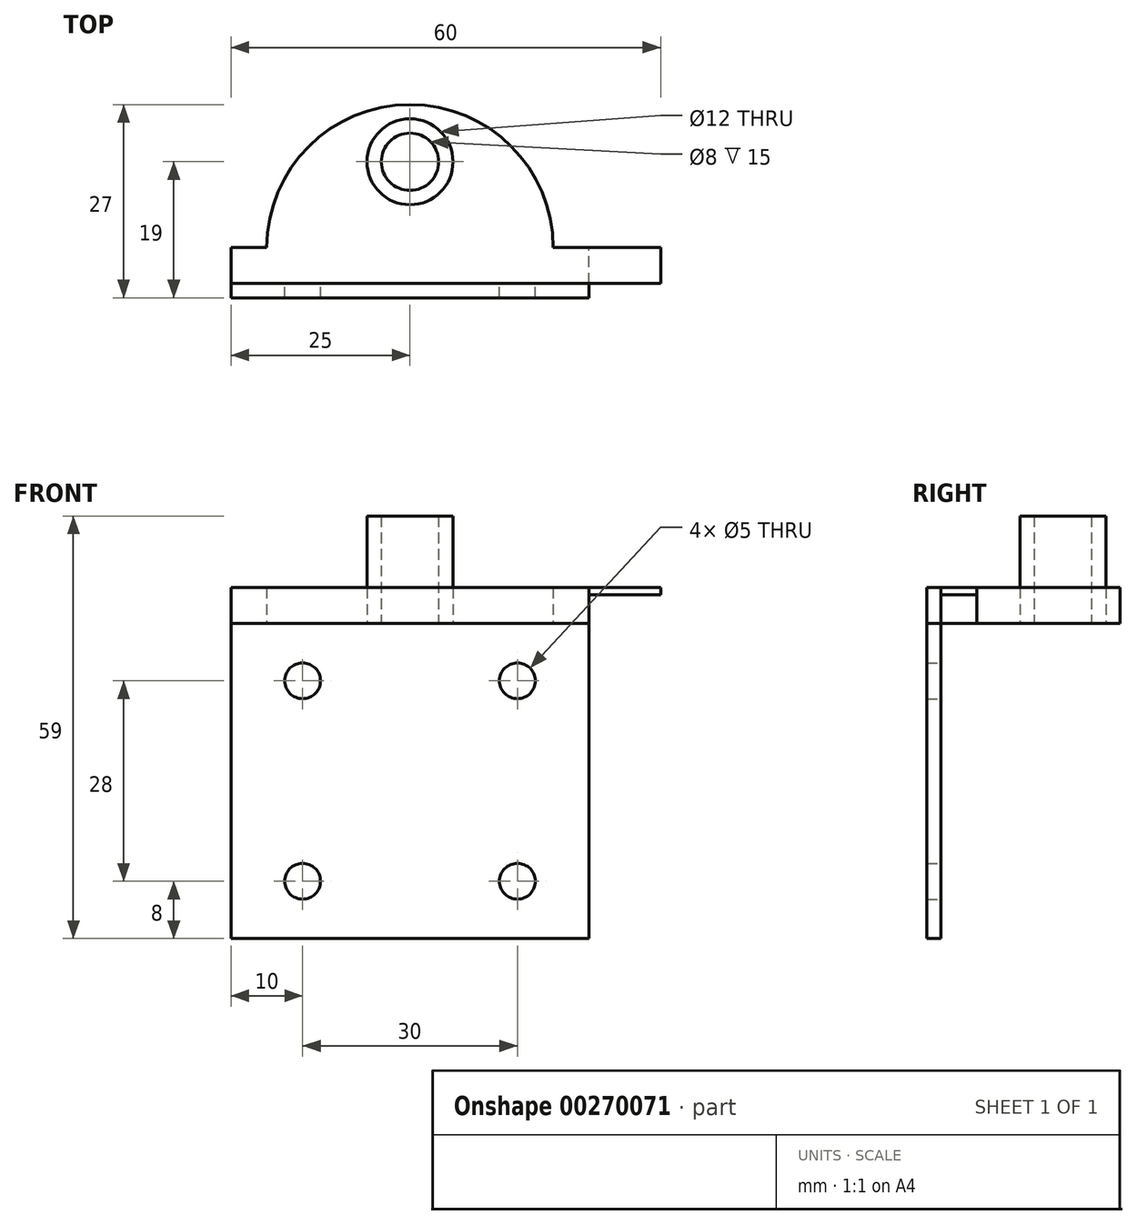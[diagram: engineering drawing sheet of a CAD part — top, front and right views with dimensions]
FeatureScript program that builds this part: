
annotation { "Feature Type Name" : "Feature", "Feature Type Description" : "" }
export const myFeature = defineFeature(function(context is Context, id is Id, definition is map)
    precondition{}
    {
        {
            var Q0;
            Q0=qCreatedBy(makeId("Front.planeOp"),FACE);
            var sketch = newSketch(context, id + "F0", { "sketchPlane" : qUnion([Q0])});
            skLineSegment(sketch, "E0.bottom", {"start": v(25, 22) * mm, "end": v(-25, 22) * mm});
            skLineSegment(sketch, "E0.top", {"start": v(25, -22) * mm, "end": v(-25, -22) * mm});
            skLineSegment(sketch, "E0.left", {"start": v(25, 22) * mm, "end": v(25, -22) * mm});
            skLineSegment(sketch, "E0.right", {"start": v(-25, 22) * mm, "end": v(-25, -22) * mm});
            skPoint(sketch, "E0.middle", {"position": v(0, 0) * mm});
            skCircle(sketch, "E1", {"center": v(-15, 14) * mm, "radius": 2.5 * mm});
            skCircle(sketch, "E2.MirrorC", {"center": v(15, 14) * mm, "radius": 2.5 * mm});
            skCircle(sketch, "E3.MirrorC", {"center": v(15, -14) * mm, "radius": 2.5 * mm});
            skCircle(sketch, "E4.MirrorC", {"center": v(-15, -14) * mm, "radius": 2.5 * mm});
            skSolve(sketch);
        }
        {
            var Q0;
            Q0=makeQuery(id+"F0.imprint","IMPRINT",FACE,{"disambiguationData":[TD([[makeQuery(id+"F0.imprint","IMPRINT",EDGE,{"derivedFrom":sQuery(id+"F0.wireOp",EDGE,"E0.bottom")}),1.0]])]});
            extrude(context, id + "F1", {"entities" : qUnion([Q0]), "depth" : 2 * mm});
        }
        {
            var Q0;
            Q0=makeQuery(id+"F1.opExtrude","SWEPT_FACE",FACE,{"disambiguationData":[OSD([sQuery(id+"F0.wireOp",EDGE,"E0.bottom")])]});
            var sketch = newSketch(context, id + "F2", { "sketchPlane" : qUnion([Q0])});
            skLineSegment(sketch, "E5.bottom", {"start": v(-25, 0) * mm, "end": v(35, 0) * mm});
            skLineSegment(sketch, "E5.top", {"start": v(-25, 5) * mm, "end": v(35, 5) * mm});
            skLineSegment(sketch, "E5.left", {"start": v(-25, 0) * mm, "end": v(-25, 5) * mm});
            skLineSegment(sketch, "E5.right", {"start": v(35, 0) * mm, "end": v(35, 5) * mm});
            skArc(sketch, "E6", {"start": v(20, 5) * mm, "mid": v(0, 25) * mm, "end": v(-20, 5) * mm});
            skPoint(sketch, "E7", {"position": v(0, 17) * mm});
            skCircle(sketch, "E8", {"center": v(0, 17) * mm, "radius": 4 * mm});
            skCircle(sketch, "E9", {"center": v(0, 17) * mm, "radius": 6 * mm});
            skSolve(sketch);
        }
        {
            var Q0;
            Q0=makeQuery(id+"F1.opExtrude","SWEPT_FACE",FACE,{"disambiguationData":[OSD([sQuery(id+"F0.wireOp",EDGE,"E0.top")])]});
            var Q1;
            {var subQ4=sQuery(id+"F2.wireOp",EDGE,"E5.left");Q1=makeQuery(id+"F2.imprint","IMPRINT",FACE,{"disambiguationData":[TD([[makeQuery(id+"F2.imprint","IMPRINT",EDGE,{"derivedFrom":subQ4}),-1.0]])]});}
            var Q2;
            {var subQ0=sQuery(id+"F2.wireOp",EDGE,"E6");Q2=makeQuery(id+"F2.imprint","IMPRINT",FACE,{"disambiguationData":[TD([[makeQuery(id+"F2.imprint","IMPRINT",EDGE,{"derivedFrom":subQ0}),1.0]])]});}
            extrude(context, id + "F3", {"entities" : qUnion([Q0, Q1, Q2]), "operationType" : NewBodyOperationType.ADD, "oppositeDirection" : true, "depth" : 5 * mm});
        }
        {
            var Q0;
            Q0=makeQuery(id+"F1.opExtrude","SWEPT_FACE",FACE,{"disambiguationData":[OSD([sQuery(id+"F0.wireOp",EDGE,"E0.bottom")])]});
            extrude(context, id + "F4", {"entities" : qUnion([Q0]), "depth" : 5 * mm});
        }
        {
            var Q0;
            Q0=makeQuery(id+"F3.opExtrude","CAP_FACE",FACE,{"disambiguationData":[OSD([sQuery(id+"F2.wireOp",EDGE,"E5.bottom"),sQuery(id+"F2.wireOp",EDGE,"E5.top"),sQuery(id+"F2.wireOp",EDGE,"E5.left"),sQuery(id+"F2.wireOp",EDGE,"E5.right"),sQuery(id+"F2.wireOp",EDGE,"E6"),sQuery(id+"F2.wireOp",EDGE,"E9")])],"isStart":true});
            var sketch = newSketch(context, id + "F5", { "sketchPlane" : qUnion([Q0])});
            skCircle(sketch, "E10", {"center": v(0, -17) * mm, "radius": 4 * mm});
            skSolve(sketch);
        }
        {
            var Q0;
            Q0=makeQuery(id+"F5.imprint","IMPRINT",FACE,{"disambiguationData":[TD([[makeQuery(id+"F5.imprint","IMPRINT",EDGE,{"derivedFrom":sQuery(id+"F5.wireOp",EDGE,"E10")}),-1.0]])]});
            extrude(context, id + "F6", {"entities" : qUnion([Q0]), "oppositeDirection" : true, "depth" : 15 * mm});
        }
        {
            var Q0;
            Q0=makeQuery(id+"F3.opExtrude","SWEPT_FACE",FACE,{"disambiguationData":[OSD([sQuery(id+"F2.wireOp",EDGE,"E5.right")])]});
            var sketch = newSketch(context, id + "F7", { "sketchPlane" : qUnion([Q0])});
            skLineSegment(sketch, "E11.bottom", {"start": v(0, 22) * mm, "end": v(5, 22) * mm});
            skLineSegment(sketch, "E11.top", {"start": v(0, 27) * mm, "end": v(5, 27) * mm});
            skLineSegment(sketch, "E11.left", {"start": v(0, 22) * mm, "end": v(0, 27) * mm});
            skLineSegment(sketch, "E11.right", {"start": v(5, 22) * mm, "end": v(5, 27) * mm});
            skLineSegment(sketch, "E12", {"start": v(0, 26) * mm, "end": v(5, 26) * mm});
            skSolve(sketch);
        }
        {
            var Q0;
            {var subQ0=sQuery(id+"F7.wireOp",EDGE,"E11.bottom");Q0=makeQuery(id+"F7.imprint","IMPRINT",FACE,{"disambiguationData":[TD([[makeQuery(id+"F7.imprint","IMPRINT",EDGE,{"derivedFrom":subQ0}),1.0]])]});}
            extrude(context, id + "F8", {"entities" : qUnion([Q0]), "operationType" : NewBodyOperationType.REMOVE, "oppositeDirection" : true, "depth" : 10 * mm});
        }
    });
